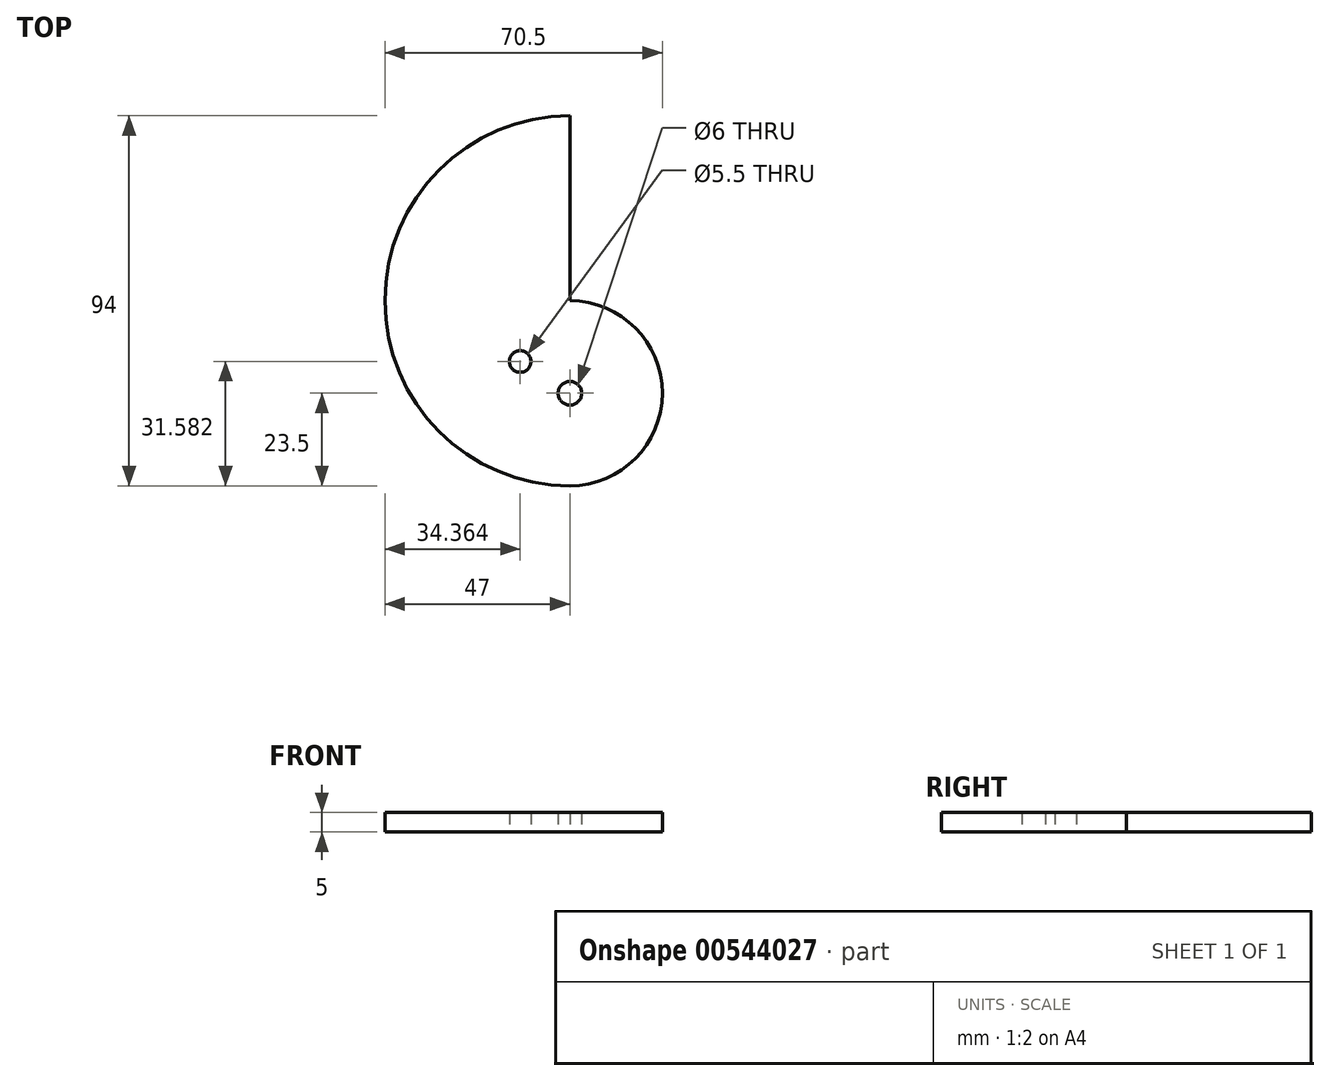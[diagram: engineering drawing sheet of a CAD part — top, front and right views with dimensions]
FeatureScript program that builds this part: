
annotation { "Feature Type Name" : "Feature", "Feature Type Description" : "" }
export const myFeature = defineFeature(function(context is Context, id is Id, definition is map)
    precondition{}
    {
        {
            var Q0;
            Q0=qCreatedBy(makeId("Top.planeOp"),FACE);
            var sketch = newSketch(context, id + "F0", { "sketchPlane" : qUnion([Q0])});
            skArc(sketch, "E0", {"start": v(0, 47) * mm, "mid": v(-47, 0) * mm, "end": v(0, -47) * mm});
            skArc(sketch, "E1", {"start": v(0, -47) * mm, "mid": v(23.5, -23.5) * mm, "end": v(0, 0) * mm});
            skLineSegment(sketch, "E2", {"start": v(0, -47) * mm, "end": v(0, 47) * mm, "construction": true});
            skLineSegment(sketch, "E3", {"start": v(0, 0) * mm, "end": v(0, 47) * mm});
            skCircle(sketch, "E4", {"center": v(0, -23.5) * mm, "radius": 3 * mm});
            skCircle(sketch, "E5", {"center": v(-12.64, -15.42) * mm, "radius": 2.75 * mm});
            skSolve(sketch);
        }
        {
            var Q0;
            Q0 = qSketchRegion(id + "F0", true);
            extrude(context, id + "F1", {"entities" : qUnion([Q0]), "depth" : 5 * mm, "offsetDistance" : 25 * mm});
        }
    });
